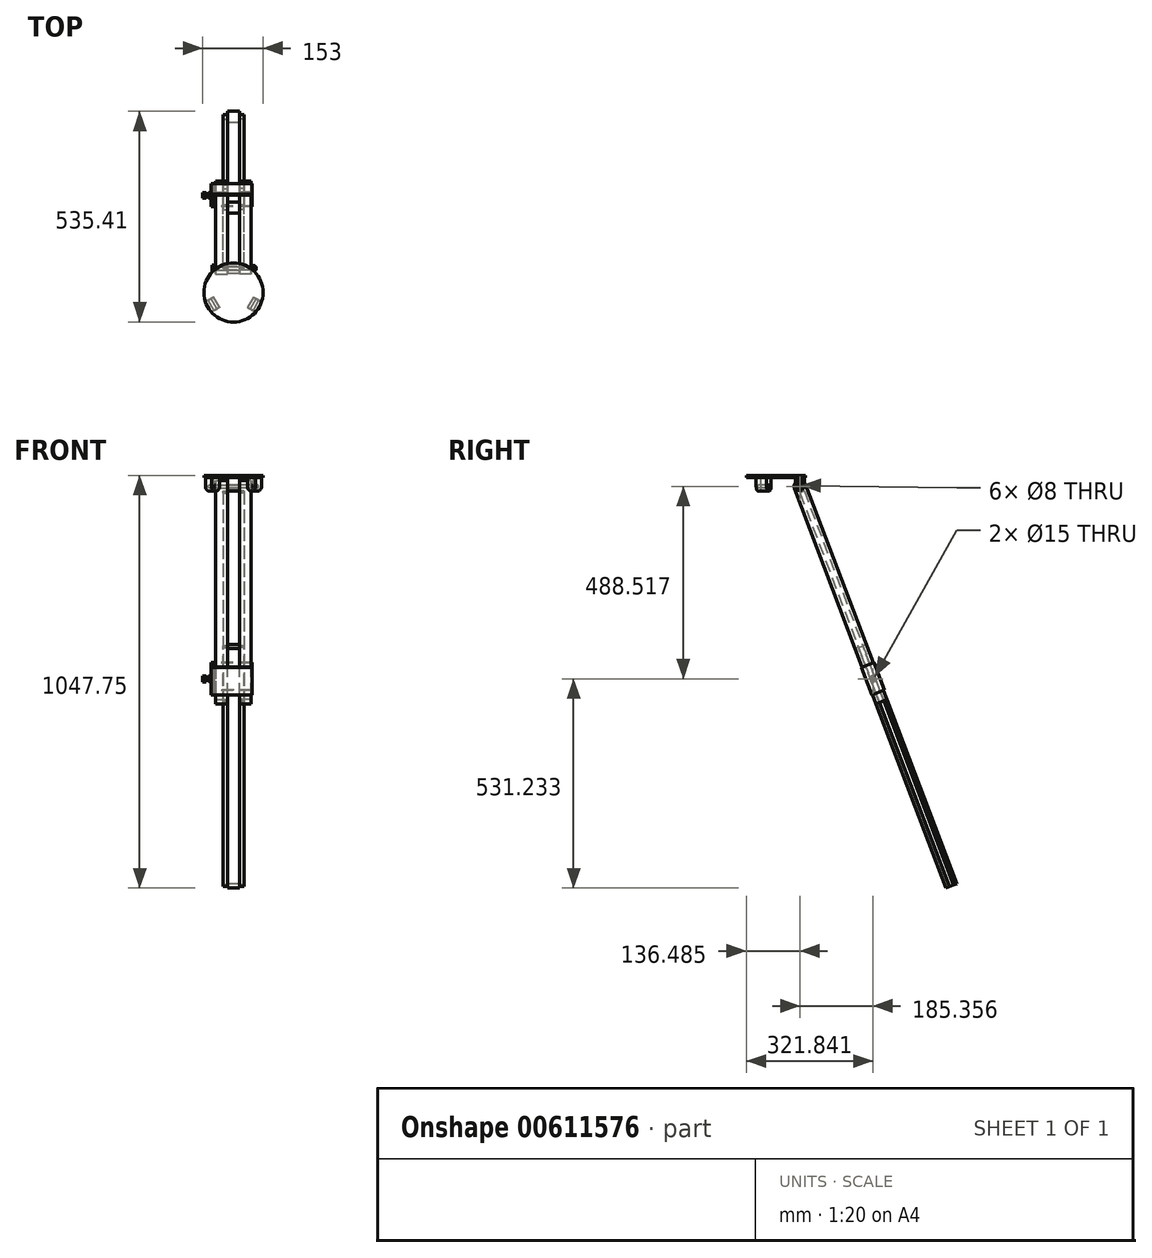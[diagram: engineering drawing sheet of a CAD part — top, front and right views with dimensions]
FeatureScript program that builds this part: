
annotation { "Feature Type Name" : "Feature", "Feature Type Description" : "" }
export const myFeature = defineFeature(function(context is Context, id is Id, definition is map)
    precondition{}
    {
        {
            var Q0;
            Q0=qCreatedBy(makeId("Top.planeOp"),FACE);
            var sketch = newSketch(context, id + "F0", { "sketchPlane" : qUnion([Q0])});
            skCircle(sketch, "E0", {"center": v(0, 0) * mm, "radius": 75 * mm});
            skSolve(sketch);
        }
        {
            var Q0;
            Q0 = qSketchRegion(id + "F0", true);
            extrude(context, id + "F1", {"entities" : qUnion([Q0]), "oppositeDirection" : true, "depth" : 5 * mm, "offsetDistance" : 25 * mm});
        }
        {
            var Q0;
            Q0=makeQuery(id+"F1.opExtrude","CAP_FACE",FACE,{"disambiguationData":[OSD([sQuery(id+"F0.wireOp",EDGE,"E0")])],"isStart":false});
            var sketch = newSketch(context, id + "F2", { "sketchPlane" : qUnion([Q0])});
            skLineSegment(sketch, "E1.bottom", {"start": v(-15, -49.48) * mm, "end": v(15, -49.48) * mm});
            skLineSegment(sketch, "E1.top", {"start": v(-15, -73.48) * mm, "end": v(15, -73.48) * mm});
            skLineSegment(sketch, "E1.left", {"start": v(-15, -49.48) * mm, "end": v(-15, -73.48) * mm});
            skLineSegment(sketch, "E1.right", {"start": v(15, -49.48) * mm, "end": v(15, -73.48) * mm});
            skPoint(sketch, "E1.middle", {"position": v(0, -61.48) * mm});
            skSolve(sketch);
        }
        {
            var Q0;
            Q0 = qSketchRegion(id + "F2", true);
            extrude(context, id + "F3", {"entities" : qUnion([Q0]), "depth" : 35 * mm, "offsetDistance" : 25 * mm});
        }
        {
            var Q0;
            Q0=makeQuery(id+"F3.opExtrude","SWEPT_FACE",FACE,{"disambiguationData":[OSD([sQuery(id+"F2.wireOp",EDGE,"E1.right")])]});
            var sketch = newSketch(context, id + "F4", { "sketchPlane" : qUnion([Q0])});
            skCircle(sketch, "E2", {"center": v(61.48, -28) * mm, "radius": 4 * mm});
            skPoint(sketch, "E2.centerSnap0", {"position": v(61.48, -40) * mm});
            skSolve(sketch);
        }
        {
            var Q0;
            Q0 = qSketchRegion(id + "F4", true);
            extrude(context, id + "F5", {"entities" : qUnion([Q0]), "operationType" : NewBodyOperationType.REMOVE, "endBound" : BoundingType.THROUGH_ALL, "oppositeDirection" : true, "depth" : 25 * mm, "offsetDistance" : 25 * mm});
        }
        {
            var Q0;
            Q0=makeQuery(id+"F3.opExtrude","CAP_EDGE",EDGE,{"disambiguationData":[OSD([sQuery(id+"F2.wireOp",EDGE,"E1.bottom")])],"isStart":false});
            var Q1;
            Q1=makeQuery(id+"F3.opExtrude","CAP_EDGE",EDGE,{"disambiguationData":[OSD([sQuery(id+"F2.wireOp",EDGE,"E1.top")])],"isStart":false});
            fillet(context, id + "F6", {"entities" : qUnion([Q0, Q1]), "radius" : 12 * mm, "tangentPropagation" : true, "allowEdgeOverflow" : false});
        }
        {
            var Q0;
            Q0=makeQuery(id+"F3.opExtrude","SWEPT_BODY",BODY,{"disambiguationData":[OSD([sQuery(id+"F2.wireOp",EDGE,"E1.bottom"),sQuery(id+"F2.wireOp",EDGE,"E1.top"),sQuery(id+"F2.wireOp",EDGE,"E1.left"),sQuery(id+"F2.wireOp",EDGE,"E1.right")])]});
            var Q1;
            Q1=makeQuery(id+"F1.opExtrude","CAP_EDGE",EDGE,{"disambiguationData":[OSD([sQuery(id+"F0.wireOp",EDGE,"E0")])],"isStart":false});
            circularPattern(context, id + "F7", {"entities" : qUnion([Q0]), "axis" : qUnion([Q1]), "angle" : 360 * degree, "instanceCount" : 3, "equalSpace" : true});
        }
        {
            var Q0;
            Q0=makeQuery(id+"F3.opExtrude","SWEPT_FACE",FACE,{"disambiguationData":[OSD([sQuery(id+"F2.wireOp",EDGE,"E1.left")])]});
            var sketch = newSketch(context, id + "F8", { "sketchPlane" : qUnion([Q0])});
            skLineSegment(sketch, "E3", {"start": v(-70.19, -8.65) * mm, "end": v(-283.04, -569.63) * mm});
            skLineSegment(sketch, "E4", {"start": v(-283.04, -569.63) * mm, "end": v(-254.99, -580.27) * mm});
            skLineSegment(sketch, "E5", {"start": v(-254.99, -580.27) * mm, "end": v(-42.14, -19.3) * mm});
            skLineSegment(sketch, "E6", {"start": v(-42.14, -19.3) * mm, "end": v(-70.19, -8.65) * mm});
            skCircle(sketch, "E7.0", {"center": v(-61.48, -28) * mm, "radius": 4 * mm});
            skLineSegment(sketch, "E8", {"start": v(-94.47, -114.94) * mm, "end": v(-37.07, 36.36) * mm, "construction": true});
            skSolve(sketch);
        }
        {
            var Q0;
            Q0 = qSketchRegion(id + "F8", true);
            extrude(context, id + "F9", {"entities" : qUnion([Q0]), "depth" : 30 * mm, "offsetDistance" : 25 * mm});
        }
        {
            var Q0;
            Q0=makeQuery(id+"F9.opExtrude","SWEPT_EDGE",EDGE,{"disambiguationData":[OSD([sQuery(id+"F8.wireOp",EDGE,"E3"),sQuery(id+"F8.wireOp",EDGE,"E6")])]});
            var Q1;
            Q1=makeQuery(id+"F9.opExtrude","SWEPT_EDGE",EDGE,{"disambiguationData":[OSD([sQuery(id+"F8.wireOp",EDGE,"E5"),sQuery(id+"F8.wireOp",EDGE,"E6")])]});
            fillet(context, id + "F10", {"entities" : qUnion([Q0, Q1]), "radius" : 15 * mm, "tangentPropagation" : true, "allowEdgeOverflow" : false});
        }
        {
            var Q0;
            Q0=makeQuery(id+"F9.opExtrude","SWEPT_FACE",FACE,{"disambiguationData":[OSD([sQuery(id+"F8.wireOp",EDGE,"E4")])]});
            var sketch = newSketch(context, id + "F11", { "sketchPlane" : qUnion([Q0])});
            skLineSegment(sketch, "E9.bottom", {"start": v(-27, -41.55) * mm, "end": v(-3, -41.55) * mm});
            skLineSegment(sketch, "E9.top", {"start": v(-27, -53.55) * mm, "end": v(-3, -53.55) * mm});
            skLineSegment(sketch, "E9.left", {"start": v(-27, -41.55) * mm, "end": v(-27, -53.55) * mm});
            skLineSegment(sketch, "E9.right", {"start": v(-3, -41.55) * mm, "end": v(-3, -53.55) * mm});
            skPoint(sketch, "E9.middle", {"position": v(-15, -47.55) * mm});
            skSolve(sketch);
        }
        {
            var Q0;
            Q0 = qSketchRegion(id + "F11", true);
            extrude(context, id + "F12", {"entities" : qUnion([Q0]), "operationType" : NewBodyOperationType.REMOVE, "oppositeDirection" : true, "depth" : 570 * mm, "offsetDistance" : 25 * mm});
        }
        {
            var Q0;
            Q0=makeQuery(id+"F9.opExtrude","SWEPT_BODY",BODY,{"disambiguationData":[OSD([sQuery(id+"F8.wireOp",EDGE,"E3"),sQuery(id+"F8.wireOp",EDGE,"E4"),sQuery(id+"F8.wireOp",EDGE,"E5"),sQuery(id+"F8.wireOp",EDGE,"E6"),sQuery(id+"F8.wireOp",EDGE,"E7.0")])]});
            var Q1;
            Q1=qCreatedBy(makeId("Right.planeOp"),FACE);
            mirror(context, id + "F13", {"entities" : qUnion([Q0]), "mirrorPlane" : qUnion([Q1])});
        }
        {
            var Q0;
            Q0=makeQuery(id+"F13.opPattern","COPY",FACE,{"derivedFrom":makeQuery(id+"F9.opExtrude","SWEPT_FACE",FACE,{"disambiguationData":[OSD([sQuery(id+"F8.wireOp",EDGE,"E4")])]}),"instanceName":"1"});
            var sketch = newSketch(context, id + "F14", { "sketchPlane" : qUnion([Q0])});
            skLineSegment(sketch, "E10", {"start": v(27, -53.55) * mm, "end": v(15, -53.55) * mm});
            skLineSegment(sketch, "E11", {"start": v(15, -53.55) * mm, "end": v(15, -62.55) * mm});
            skLineSegment(sketch, "E12", {"start": v(15, -62.55) * mm, "end": v(-15, -62.55) * mm});
            skLineSegment(sketch, "E13", {"start": v(-15, -62.55) * mm, "end": v(-15, -53.55) * mm});
            skLineSegment(sketch, "E14", {"start": v(-15, -53.55) * mm, "end": v(-27, -53.55) * mm});
            skLineSegment(sketch, "E15", {"start": v(-27, -53.55) * mm, "end": v(-27, -41.55) * mm});
            skLineSegment(sketch, "E16", {"start": v(-27, -41.55) * mm, "end": v(-15, -41.55) * mm});
            skLineSegment(sketch, "E17", {"start": v(-15, -41.55) * mm, "end": v(-15, -32.55) * mm});
            skLineSegment(sketch, "E18", {"start": v(-15, -32.55) * mm, "end": v(15, -32.55) * mm});
            skLineSegment(sketch, "E19", {"start": v(15, -32.55) * mm, "end": v(15, -41.55) * mm});
            skLineSegment(sketch, "E20", {"start": v(15, -41.55) * mm, "end": v(27, -41.55) * mm});
            skLineSegment(sketch, "E21", {"start": v(27, -41.55) * mm, "end": v(27, -53.55) * mm});
            skSolve(sketch);
        }
        {
            var Q0;
            Q0 = qSketchRegion(id + "F14", true);
            extrude(context, id + "F15", {"entities" : qUnion([Q0]), "depth" : 500 * mm, "offsetDistance" : 25 * mm, "hasSecondDirection" : true, "secondDirectionOppositeDirection" : true, "secondDirectionDepth" : 150 * mm});
        }
        {
            var Q0;
            Q0=makeQuery(id+"F9.opExtrude","CAP_FACE",FACE,{"disambiguationData":[OSD([sQuery(id+"F8.wireOp",EDGE,"E3"),sQuery(id+"F8.wireOp",EDGE,"E4"),sQuery(id+"F8.wireOp",EDGE,"E5"),sQuery(id+"F8.wireOp",EDGE,"E6"),sQuery(id+"F8.wireOp",EDGE,"E7.0")])],"isStart":false});
            var sketch = newSketch(context, id + "F16", { "sketchPlane" : qUnion([Q0])});
            skCircle(sketch, "E22.0", {"center": v(-61.48, -28) * mm, "radius": 4 * mm});
            skCircle(sketch, "E23", {"center": v(-61.48, -28) * mm, "radius": 10 * mm});
            skSolve(sketch);
        }
        {
            var Q0;
            Q0 = qSketchRegion(id + "F16", true);
            extrude(context, id + "F17", {"entities" : qUnion([Q0]), "depth" : 2 * mm, "offsetDistance" : 25 * mm});
        }
        {
            var Q0;
            Q0=makeQuery(id+"F17.opExtrude","SWEPT_BODY",BODY,{"disambiguationData":[OSD([sQuery(id+"F16.wireOp",EDGE,"E22.0"),sQuery(id+"F16.wireOp",EDGE,"E23")])]});
            var Q1;
            Q1=qCreatedBy(makeId("Right.planeOp"),FACE);
            mirror(context, id + "F18", {"entities" : qUnion([Q0]), "mirrorPlane" : qUnion([Q1])});
        }
        {
            var Q0;
            Q0=makeQuery(id+"F17.opExtrude","CAP_FACE",FACE,{"disambiguationData":[OSD([sQuery(id+"F16.wireOp",EDGE,"E22.0"),sQuery(id+"F16.wireOp",EDGE,"E23")])],"isStart":false});
            var sketch = newSketch(context, id + "F19", { "sketchPlane" : qUnion([Q0])});
            skCircle(sketch, "E24.0", {"center": v(-61.48, -28) * mm, "radius": 4 * mm});
            skSolve(sketch);
        }
        {
            var Q0;
            Q0 = qSketchRegion(id + "F19", true);
            extrude(context, id + "F20", {"entities" : qUnion([Q0]), "oppositeDirection" : true, "depth" : 104 * mm, "offsetDistance" : 25 * mm});
        }
        {
            var Q0;
            Q0=makeQuery(id+"F20.opExtrude","CAP_FACE",FACE,{"disambiguationData":[OSD([sQuery(id+"F19.wireOp",EDGE,"E24.0")])],"isStart":true});
            var sketch = newSketch(context, id + "F21", { "sketchPlane" : qUnion([Q0])});
            skCircle(sketch, "E25.cCircle", {"center": v(-61.48, -28) * mm, "radius": 6.5 * mm, "construction": true});
            skLineSegment(sketch, "E25.0", {"start": v(-57.73, -34.5) * mm, "end": v(-65.24, -34.5) * mm});
            skLineSegment(sketch, "E25.1", {"start": v(-65.24, -34.5) * mm, "end": v(-69, -28) * mm});
            skLineSegment(sketch, "E25.2", {"start": v(-69, -28) * mm, "end": v(-65.24, -21.5) * mm});
            skLineSegment(sketch, "E25.3", {"start": v(-65.24, -21.5) * mm, "end": v(-57.73, -21.5) * mm});
            skLineSegment(sketch, "E25.4", {"start": v(-57.73, -21.5) * mm, "end": v(-53.98, -28) * mm});
            skLineSegment(sketch, "E25.5", {"start": v(-53.98, -28) * mm, "end": v(-57.73, -34.5) * mm});
            skPoint(sketch, "E25.0.midPoint", {"position": v(-61.48, -34.5) * mm});
            skSolve(sketch);
        }
        {
            var Q0;
            Q0 = qSketchRegion(id + "F21", true);
            extrude(context, id + "F22", {"entities" : qUnion([Q0]), "operationType" : NewBodyOperationType.ADD, "depth" : 8 * mm, "offsetDistance" : 25 * mm});
        }
        {
            var Q0;
            Q0=makeQuery(id+"F18.opPattern","COPY",FACE,{"derivedFrom":makeQuery(id+"F17.opExtrude","CAP_FACE",FACE,{"disambiguationData":[OSD([sQuery(id+"F16.wireOp",EDGE,"E22.0"),sQuery(id+"F16.wireOp",EDGE,"E23")])],"isStart":false}),"instanceName":"1"});
            var sketch = newSketch(context, id + "F23", { "sketchPlane" : qUnion([Q0])});
            skCircle(sketch, "E26.0", {"center": v(61.48, -28) * mm, "radius": 4 * mm});
            skCircle(sketch, "E27.cCircle", {"center": v(61.48, -28) * mm, "radius": 6.5 * mm, "construction": true});
            skLineSegment(sketch, "E27.0", {"start": v(68.93, -27.07) * mm, "end": v(66.01, -33.99) * mm});
            skLineSegment(sketch, "E27.1", {"start": v(66.01, -33.99) * mm, "end": v(58.57, -34.91) * mm});
            skLineSegment(sketch, "E27.2", {"start": v(58.57, -34.91) * mm, "end": v(54.04, -28.93) * mm});
            skLineSegment(sketch, "E27.3", {"start": v(54.04, -28.93) * mm, "end": v(56.96, -22.01) * mm});
            skLineSegment(sketch, "E27.4", {"start": v(56.96, -22.01) * mm, "end": v(64.4, -21.09) * mm});
            skLineSegment(sketch, "E27.5", {"start": v(64.4, -21.09) * mm, "end": v(68.93, -27.07) * mm});
            skPoint(sketch, "E27.0.midPoint", {"position": v(67.47, -30.53) * mm});
            skSolve(sketch);
        }
        {
            var Q0;
            Q0 = qSketchRegion(id + "F23", true);
            extrude(context, id + "F24", {"entities" : qUnion([Q0]), "depth" : 8 * mm, "offsetDistance" : 25 * mm});
        }
        {
            var Q0;
            Q0=makeQuery(id+"F13.opPattern","COPY",FACE,{"derivedFrom":makeQuery(id+"F9.opExtrude","SWEPT_FACE",FACE,{"disambiguationData":[OSD([sQuery(id+"F8.wireOp",EDGE,"E4")])]}),"instanceName":"1"});
            cPlane(context, id + "F25", {"entities" : qUnion([Q0]), "cplaneType" : CPlaneType.OFFSET, "offset" : 25 * mm, "oppositeDirection" : true, "width" : 150 * mm, "height" : 150 * mm});
        }
        {
            var Q0;
            Q0=qCreatedBy(id+"F25.planeOp",FACE);
            var sketch = newSketch(context, id + "F26", { "sketchPlane" : qUnion([Q0])});
            skLineSegment(sketch, "E28.bottom", {"start": v(45, -62.55) * mm, "end": v(-55, -62.55) * mm});
            skLineSegment(sketch, "E28.top", {"start": v(45, -32.55) * mm, "end": v(-55, -32.55) * mm});
            skLineSegment(sketch, "E28.left", {"start": v(45, -62.55) * mm, "end": v(45, -32.55) * mm});
            skLineSegment(sketch, "E28.right", {"start": v(-55, -62.55) * mm, "end": v(-55, -32.55) * mm});
            skLineSegment(sketch, "E29.bottom", {"start": v(47, -64.55) * mm, "end": v(-57, -64.55) * mm});
            skLineSegment(sketch, "E29.top", {"start": v(47, -30.55) * mm, "end": v(-57, -30.55) * mm});
            skLineSegment(sketch, "E29.left", {"start": v(47, -64.55) * mm, "end": v(47, -30.55) * mm});
            skLineSegment(sketch, "E29.right", {"start": v(-57, -64.55) * mm, "end": v(-57, -30.55) * mm});
            skSolve(sketch);
        }
        {
            var Q0;
            Q0 = qSketchRegion(id + "F26", true);
            extrude(context, id + "F27", {"entities" : qUnion([Q0]), "oppositeDirection" : true, "depth" : 75 * mm, "offsetDistance" : 25 * mm});
        }
        {
            var Q0;
            Q0=qCreatedBy(id+"F25.planeOp",FACE);
            var sketch = newSketch(context, id + "F28", { "sketchPlane" : qUnion([Q0])});
            skLineSegment(sketch, "E30.bottom", {"start": v(-45, -62.55) * mm, "end": v(-48, -62.55) * mm});
            skLineSegment(sketch, "E30.top", {"start": v(-45, -32.55) * mm, "end": v(-48, -32.55) * mm});
            skLineSegment(sketch, "E30.left", {"start": v(-45, -62.55) * mm, "end": v(-45, -32.55) * mm});
            skLineSegment(sketch, "E30.right", {"start": v(-48, -62.55) * mm, "end": v(-48, -32.55) * mm});
            skLineSegment(sketch, "E31.bottom", {"start": v(-52, -62.55) * mm, "end": v(-55, -62.55) * mm});
            skLineSegment(sketch, "E31.top", {"start": v(-52, -32.55) * mm, "end": v(-55, -32.55) * mm});
            skLineSegment(sketch, "E31.left", {"start": v(-52, -62.55) * mm, "end": v(-52, -32.55) * mm});
            skLineSegment(sketch, "E31.right", {"start": v(-55, -62.55) * mm, "end": v(-55, -32.55) * mm});
            skSolve(sketch);
        }
        {
            var Q0;
            Q0 = qSketchRegion(id + "F28", true);
            extrude(context, id + "F29", {"entities" : qUnion([Q0]), "oppositeDirection" : true, "depth" : 75 * mm, "offsetDistance" : 25 * mm});
        }
        {
            var Q0;
            Q0=makeQuery(id+"F27.opExtrude","SWEPT_FACE",FACE,{"disambiguationData":[OSD([sQuery(id+"F26.wireOp",EDGE,"E29.right")])]});
            var sketch = newSketch(context, id + "F30", { "sketchPlane" : qUnion([Q0])});
            skCircle(sketch, "E32", {"center": v(-246.84, -516.52) * mm, "radius": 4 * mm});
            skLineSegment(sketch, "E33", {"start": v(-246.84, -516.52) * mm, "end": v(-254.1, -535.64) * mm, "construction": true});
            skLineSegment(sketch, "E34", {"start": v(-246.84, -516.52) * mm, "end": v(-215.92, -528.25) * mm, "construction": true});
            skSolve(sketch);
        }
        {
            var Q0;
            Q0 = qSketchRegion(id + "F30", true);
            var Q1;
            Q1=makeQuery(id+"F29.opExtrude","SWEPT_BODY",BODY,{"disambiguationData":[OSD([sQuery(id+"F28.wireOp",EDGE,"E30.bottom"),sQuery(id+"F28.wireOp",EDGE,"E30.top"),sQuery(id+"F28.wireOp",EDGE,"E30.left"),sQuery(id+"F28.wireOp",EDGE,"E30.right")])]});
            extrude(context, id + "F31", {"entities" : qUnion([Q0]), "operationType" : NewBodyOperationType.REMOVE, "endBound" : BoundingType.UP_TO_BODY, "oppositeDirection" : true, "depth" : 25 * mm, "endBoundEntityBody" : qUnion([Q1]), "offsetDistance" : 25 * mm});
        }
        {
            var Q0;
            Q0=makeQuery(id+"F27.opExtrude","SWEPT_FACE",FACE,{"disambiguationData":[OSD([sQuery(id+"F26.wireOp",EDGE,"E29.right")])]});
            var sketch = newSketch(context, id + "F32", { "sketchPlane" : qUnion([Q0])});
            skCircle(sketch, "E35", {"center": v(-246.84, -516.52) * mm, "radius": 7.5 * mm});
            skSolve(sketch);
        }
        {
            var Q0;
            Q0 = qSketchRegion(id + "F32", true);
            extrude(context, id + "F33", {"entities" : qUnion([Q0]), "operationType" : NewBodyOperationType.REMOVE, "endBound" : BoundingType.UP_TO_NEXT, "oppositeDirection" : true, "depth" : 25 * mm, "offsetDistance" : 25 * mm});
        }
        {
            var Q0;
            Q0=makeQuery(id+"F29.opExtrude","SWEPT_FACE",FACE,{"disambiguationData":[OSD([sQuery(id+"F28.wireOp",EDGE,"E31.right")])]});
            var sketch = newSketch(context, id + "F34", { "sketchPlane" : qUnion([Q0])});
            skCircle(sketch, "E36.0", {"center": v(-246.84, -516.52) * mm, "radius": 4 * mm});
            skSolve(sketch);
        }
        {
            var Q0;
            Q0 = qSketchRegion(id + "F34", true);
            var Q1;
            Q1=makeQuery(id+"F29.opExtrude","SWEPT_BODY",BODY,{"disambiguationData":[OSD([sQuery(id+"F28.wireOp",EDGE,"E30.bottom"),sQuery(id+"F28.wireOp",EDGE,"E30.top"),sQuery(id+"F28.wireOp",EDGE,"E30.left"),sQuery(id+"F28.wireOp",EDGE,"E30.right")])]});
            extrude(context, id + "F35", {"entities" : qUnion([Q0]), "endBound" : BoundingType.UP_TO_BODY, "oppositeDirection" : true, "depth" : 25 * mm, "endBoundEntityBody" : qUnion([Q1]), "offsetDistance" : 25 * mm, "hasSecondDirection" : true, "secondDirectionOppositeDirection" : false, "secondDirectionDepth" : 15 * mm});
        }
        {
            var Q0;
            Q0=makeQuery(id+"F29.opExtrude","SWEPT_FACE",FACE,{"disambiguationData":[OSD([sQuery(id+"F28.wireOp",EDGE,"E31.right")])]});
            var sketch = newSketch(context, id + "F36", { "sketchPlane" : qUnion([Q0])});
            skCircle(sketch, "E37.0", {"center": v(-246.84, -516.52) * mm, "radius": 4 * mm});
            skCircle(sketch, "E38.cCircle", {"center": v(-246.84, -516.52) * mm, "radius": 6.5 * mm, "construction": true});
            skLineSegment(sketch, "E38.0", {"start": v(-239.34, -516.81) * mm, "end": v(-243.35, -523.16) * mm});
            skLineSegment(sketch, "E38.1", {"start": v(-243.35, -523.16) * mm, "end": v(-250.85, -522.86) * mm});
            skLineSegment(sketch, "E38.2", {"start": v(-250.85, -522.86) * mm, "end": v(-254.34, -516.22) * mm});
            skLineSegment(sketch, "E38.3", {"start": v(-254.34, -516.22) * mm, "end": v(-250.33, -509.87) * mm});
            skLineSegment(sketch, "E38.4", {"start": v(-250.33, -509.87) * mm, "end": v(-242.83, -510.17) * mm});
            skLineSegment(sketch, "E38.5", {"start": v(-242.83, -510.17) * mm, "end": v(-239.34, -516.81) * mm});
            skPoint(sketch, "E38.0.midPoint", {"position": v(-241.34, -519.99) * mm});
            skSolve(sketch);
        }
        {
            var Q0;
            Q0 = qSketchRegion(id + "F36", true);
            extrude(context, id + "F37", {"entities" : qUnion([Q0]), "depth" : 8 * mm, "offsetDistance" : 25 * mm});
        }
        {
            var Q0;
            Q0=makeQuery(id+"F35.opExtrude","CAP_FACE",FACE,{"disambiguationData":[OSD([sQuery(id+"F34.wireOp",EDGE,"E36.0")])],"isStart":true});
            var sketch = newSketch(context, id + "F38", { "sketchPlane" : qUnion([Q0])});
            skCircle(sketch, "E39.cCircle", {"center": v(-246.84, -516.52) * mm, "radius": 6.5 * mm, "construction": true});
            skLineSegment(sketch, "E39.0", {"start": v(-240.34, -512.76) * mm, "end": v(-240.34, -520.27) * mm});
            skLineSegment(sketch, "E39.1", {"start": v(-240.34, -520.27) * mm, "end": v(-246.84, -524.02) * mm});
            skLineSegment(sketch, "E39.2", {"start": v(-246.84, -524.02) * mm, "end": v(-253.34, -520.27) * mm});
            skLineSegment(sketch, "E39.3", {"start": v(-253.34, -520.27) * mm, "end": v(-253.34, -512.76) * mm});
            skLineSegment(sketch, "E39.4", {"start": v(-253.34, -512.76) * mm, "end": v(-246.84, -509.01) * mm});
            skLineSegment(sketch, "E39.5", {"start": v(-246.84, -509.01) * mm, "end": v(-240.34, -512.76) * mm});
            skPoint(sketch, "E39.0.midPoint", {"position": v(-240.34, -516.52) * mm});
            skSolve(sketch);
        }
        {
            var Q0;
            Q0 = qSketchRegion(id + "F38", true);
            extrude(context, id + "F39", {"entities" : qUnion([Q0]), "operationType" : NewBodyOperationType.ADD, "depth" : 8 * mm, "offsetDistance" : 25 * mm});
        }
    });
